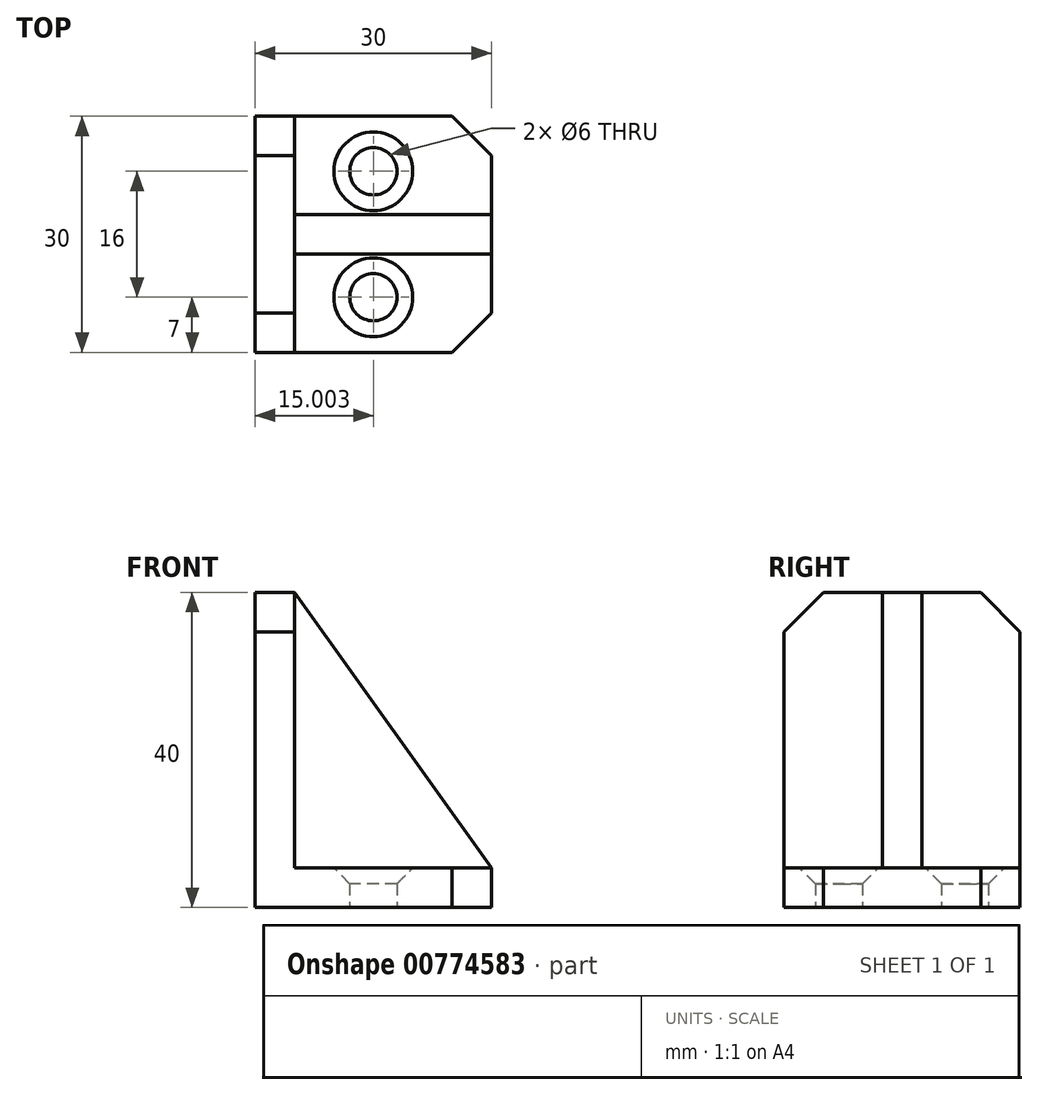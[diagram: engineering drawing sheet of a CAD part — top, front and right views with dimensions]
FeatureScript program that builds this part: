
annotation { "Feature Type Name" : "Feature", "Feature Type Description" : "" }
export const myFeature = defineFeature(function(context is Context, id is Id, definition is map)
    precondition{}
    {
        {
            var Q0;
            Q0=qCreatedBy(makeId("Top.planeOp"),FACE);
            var sketch = newSketch(context, id + "F0", { "sketchPlane" : qUnion([Q0])});
            skLineSegment(sketch, "E0", {"start": v(-117.96, 8) * mm, "end": v(-51.4, 8) * mm, "construction": true});
            skLineSegment(sketch, "E1", {"start": v(-89.04, 41.85) * mm, "end": v(-89.04, -30.86) * mm, "construction": true});
            skLineSegment(sketch, "E2.bottom", {"start": v(-104.04, 23) * mm, "end": v(-74.04, 23) * mm});
            skLineSegment(sketch, "E2.top", {"start": v(-104.04, -7) * mm, "end": v(-74.04, -7) * mm});
            skLineSegment(sketch, "E2.left", {"start": v(-104.04, 23) * mm, "end": v(-104.04, -7) * mm});
            skLineSegment(sketch, "E2.right", {"start": v(-74.04, 23) * mm, "end": v(-74.04, -7) * mm});
            skCircle(sketch, "E3", {"center": v(-89.04, 0) * mm, "radius": 3 * mm});
            skCircle(sketch, "E4", {"center": v(-89.04, 16) * mm, "radius": 3 * mm});
            skSolve(sketch);
        }
        {
            var Q0;
            Q0 = qSketchRegion(id + "F0", true);
            extrude(context, id + "F1", {"entities" : qUnion([Q0]), "depth" : 5 * mm, "offsetDistance" : 25 * mm});
        }
        {
            var Q0;
            Q0=makeQuery(id+"F1.opExtrude","SWEPT_FACE",FACE,{"disambiguationData":[OSD([sQuery(id+"F0.wireOp",EDGE,"E2.left")])]});
            var sketch = newSketch(context, id + "F2", { "sketchPlane" : qUnion([Q0])});
            skLineSegment(sketch, "E5.bottom", {"start": v(-23, 5) * mm, "end": v(7, 5) * mm});
            skLineSegment(sketch, "E5.top", {"start": v(-23, 40) * mm, "end": v(7, 40) * mm});
            skLineSegment(sketch, "E5.left", {"start": v(-23, 5) * mm, "end": v(-23, 40) * mm});
            skLineSegment(sketch, "E5.right", {"start": v(7, 5) * mm, "end": v(7, 40) * mm});
            skSolve(sketch);
        }
        {
            var Q0;
            Q0=makeQuery(id+"F2.imprint","IMPRINT",FACE,{"disambiguationData":[TD([[makeQuery(id+"F2.imprint","IMPRINT",EDGE,{"derivedFrom":sQuery(id+"F2.wireOp",EDGE,"E5.bottom")}),1.0]])]});
            extrude(context, id + "F3", {"entities" : qUnion([Q0]), "operationType" : NewBodyOperationType.ADD, "oppositeDirection" : true, "depth" : 5 * mm, "offsetDistance" : 25 * mm});
        }
        {
            var Q0;
            Q0=sQuery(id+"F0.wireOp",EDGE,"E0");
            cPlane(context, id + "F4", {"entities" : qUnion([Q0]), "cplaneType" : CPlaneType.LINE_ANGLE, "offset" : 25 * mm, "angle" : 0 * degree, "width" : 150 * mm, "height" : 150 * mm});
        }
        {
            var Q0;
            Q0=qCreatedBy(id+"F4.planeOp",FACE);
            var sketch = newSketch(context, id + "F5", { "sketchPlane" : qUnion([Q0])});
            skLineSegment(sketch, "E6", {"start": v(99.04, 40) * mm, "end": v(74.04, 5) * mm});
            skLineSegment(sketch, "E7", {"start": v(99.04, 40) * mm, "end": v(99.04, 5) * mm});
            skLineSegment(sketch, "E8", {"start": v(99.04, 5) * mm, "end": v(74.04, 5) * mm});
            skSolve(sketch);
        }
        {
            var Q0;
            Q0=makeQuery(id+"F5.imprint","IMPRINT",FACE,{"disambiguationData":[TD([[makeQuery(id+"F5.imprint","IMPRINT",EDGE,{"derivedFrom":sQuery(id+"F5.wireOp",EDGE,"E6")}),1.0]])]});
            extrude(context, id + "F6", {"entities" : qUnion([Q0]), "operationType" : NewBodyOperationType.ADD, "depth" : 5 * mm, "offsetDistance" : 25 * mm, "symmetric" : true});
        }
        {
            var Q0;
            Q0=makeQuery(id+"F3.opExtrude","SWEPT_EDGE",EDGE,{"disambiguationData":[OSD([sQuery(id+"F2.wireOp",EDGE,"E5.top"),sQuery(id+"F2.wireOp",EDGE,"E5.right")])]});
            var Q1;
            Q1=makeQuery(id+"F3.opExtrude","SWEPT_EDGE",EDGE,{"disambiguationData":[OSD([sQuery(id+"F2.wireOp",EDGE,"E5.top"),sQuery(id+"F2.wireOp",EDGE,"E5.left")])]});
            var Q2;
            Q2=makeQuery(id+"F1.opExtrude","SWEPT_EDGE",EDGE,{"disambiguationData":[OSD([sQuery(id+"F0.wireOp",EDGE,"E2.top"),sQuery(id+"F0.wireOp",EDGE,"E2.right")])]});
            var Q3;
            Q3=makeQuery(id+"F1.opExtrude","SWEPT_EDGE",EDGE,{"disambiguationData":[OSD([sQuery(id+"F0.wireOp",EDGE,"E2.bottom"),sQuery(id+"F0.wireOp",EDGE,"E2.right")])]});
            chamfer(context, id + "F7", {"entities" : qUnion([Q0, Q1, Q2, Q3]), "width" : 5 * mm, "tangentPropagation" : true});
        }
        {
            var Q0;
            {var subQ0=sQuery(id+"F0.wireOp",EDGE,"E3");Q0=makeQuery(id+"F6.boolean.opBoolean","SPLIT",EDGE,{"disambiguationData":[topologyDisambiguationEdgeConnected([makeQuery(id+"F1.opExtrude","CAP_FACE",FACE,{"disambiguationData":[OSD([sQuery(id+"F0.wireOp",EDGE,"E2.bottom"),sQuery(id+"F0.wireOp",EDGE,"E2.top"),sQuery(id+"F0.wireOp",EDGE,"E2.left"),sQuery(id+"F0.wireOp",EDGE,"E2.right"),subQ0,sQuery(id+"F0.wireOp",EDGE,"E4")])],"isStart":false})])],"derivedFrom":makeQuery(id+"F1.opExtrude","CAP_EDGE",EDGE,{"disambiguationData":[OSD([subQ0])],"isStart":false})});}
            var Q1;
            {var subQ0=sQuery(id+"F0.wireOp",EDGE,"E4");Q1=makeQuery(id+"F6.boolean.opBoolean","SPLIT",EDGE,{"disambiguationData":[topologyDisambiguationEdgeConnected([makeQuery(id+"F1.opExtrude","CAP_FACE",FACE,{"disambiguationData":[OSD([sQuery(id+"F0.wireOp",EDGE,"E2.bottom"),sQuery(id+"F0.wireOp",EDGE,"E2.top"),sQuery(id+"F0.wireOp",EDGE,"E2.left"),sQuery(id+"F0.wireOp",EDGE,"E2.right"),sQuery(id+"F0.wireOp",EDGE,"E3"),subQ0])],"isStart":false})])],"derivedFrom":makeQuery(id+"F1.opExtrude","CAP_EDGE",EDGE,{"disambiguationData":[OSD([subQ0])],"isStart":false})});}
            chamfer(context, id + "F8", {"entities" : qUnion([Q0, Q1]), "width" : 2 * mm, "tangentPropagation" : true});
        }
    });
